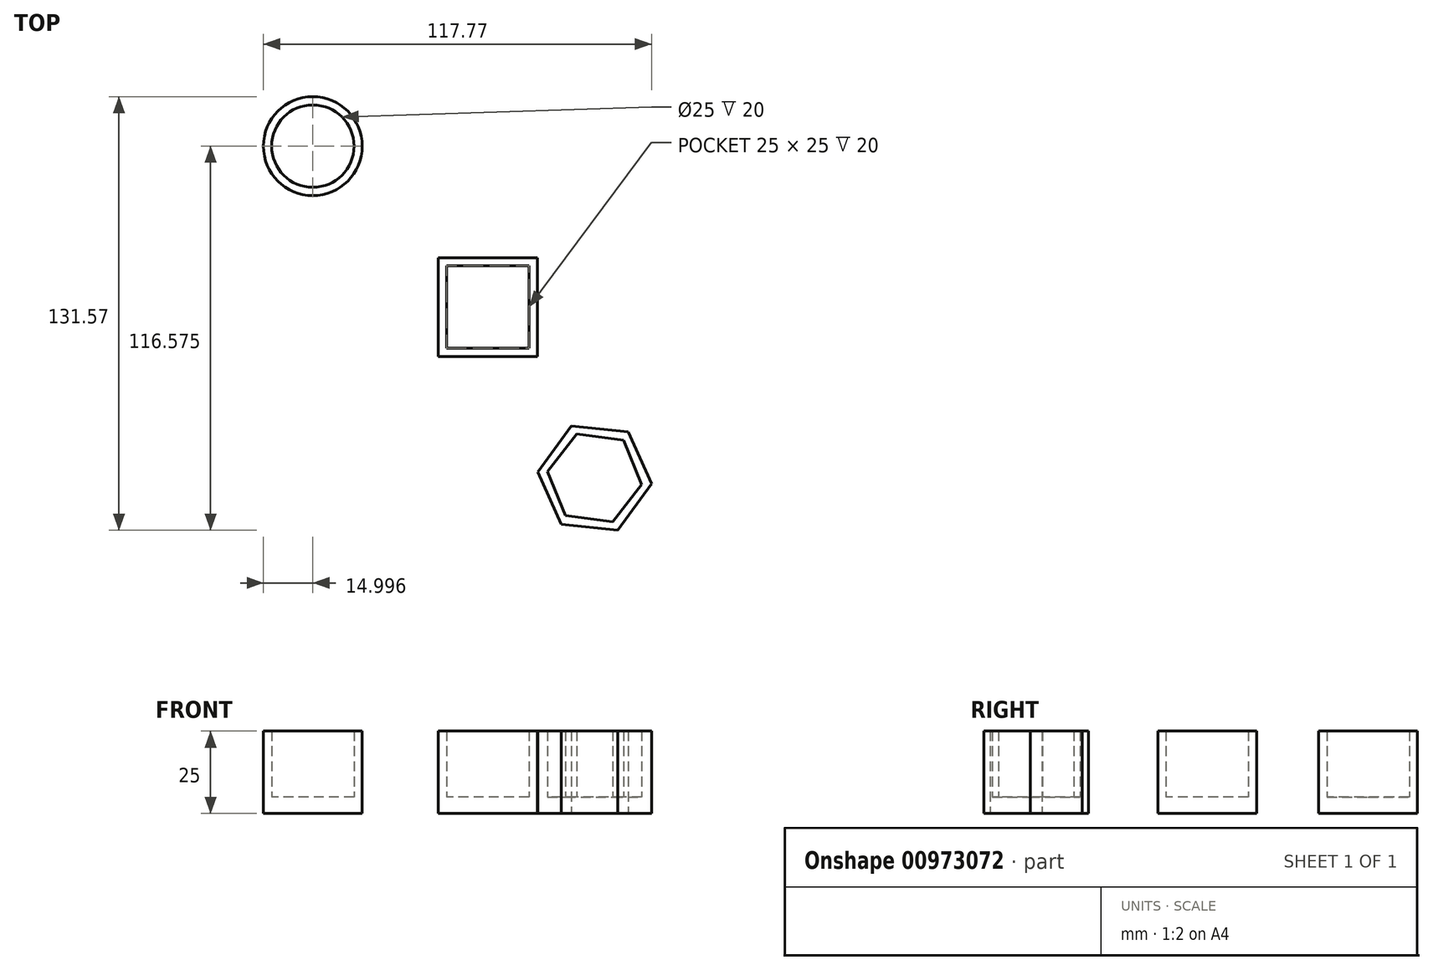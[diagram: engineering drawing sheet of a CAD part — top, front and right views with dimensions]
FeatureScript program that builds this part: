
annotation { "Feature Type Name" : "Feature", "Feature Type Description" : "" }
export const myFeature = defineFeature(function(context is Context, id is Id, definition is map)
    precondition{}
    {
        {
            var Q0;
            Q0=qCreatedBy(makeId("Top.planeOp"),FACE);
            var sketch = newSketch(context, id + "F0", { "sketchPlane" : qUnion([Q0])});
            skLineSegment(sketch, "E0.bottom", {"start": v(15, -15) * mm, "end": v(-15, -15) * mm});
            skLineSegment(sketch, "E0.top", {"start": v(15, 15) * mm, "end": v(-15, 15) * mm});
            skLineSegment(sketch, "E0.left", {"start": v(15, -15) * mm, "end": v(15, 15) * mm});
            skLineSegment(sketch, "E0.right", {"start": v(-15, -15) * mm, "end": v(-15, 15) * mm});
            skPoint(sketch, "E0.middle", {"position": v(0, 0) * mm});
            skLineSegment(sketch, "E1.bottom", {"start": v(-12.5, -12.5) * mm, "end": v(12.5, -12.5) * mm});
            skLineSegment(sketch, "E1.top", {"start": v(-12.5, 12.5) * mm, "end": v(12.5, 12.5) * mm});
            skLineSegment(sketch, "E1.left", {"start": v(-12.5, -12.5) * mm, "end": v(-12.5, 12.5) * mm});
            skLineSegment(sketch, "E1.right", {"start": v(12.5, -12.5) * mm, "end": v(12.5, 12.5) * mm});
            skSolve(sketch);
        }
        {
            var Q0;
            Q0=makeQuery(id+"F0.imprint","IMPRINT",FACE,{"disambiguationData":[TD([[makeQuery(id+"F0.imprint","IMPRINT",EDGE,{"derivedFrom":sQuery(id+"F0.wireOp",EDGE,"E0.bottom")}),-1.0]])]});
            var Q1;
            Q1=makeQuery(id+"F0.imprint","IMPRINT",FACE,{"disambiguationData":[TD([[makeQuery(id+"F0.imprint","IMPRINT",EDGE,{"derivedFrom":sQuery(id+"F0.wireOp",EDGE,"E1.bottom")}),1.0]])]});
            extrude(context, id + "F1", {"entities" : qUnion([Q0, Q1]), "depth" : 5 * mm, "offsetDistance" : 25 * mm});
        }
        {
            var Q0;
            Q0 = qSketchRegion(id + "F0", true);
            extrude(context, id + "F2", {"entities" : qUnion([Q0]), "operationType" : NewBodyOperationType.ADD, "depth" : 25 * mm, "offsetDistance" : 25 * mm});
        }
        {
            var Q0;
            Q0=qCreatedBy(makeId("Top.planeOp"),FACE);
            var sketch = newSketch(context, id + "F3", { "sketchPlane" : qUnion([Q0])});
            skCircle(sketch, "E2", {"center": v(-53.11, 48.86) * mm, "radius": 15 * mm});
            skCircle(sketch, "E3", {"center": v(-53.11, 48.86) * mm, "radius": 12.5 * mm});
            skSolve(sketch);
        }
        {
            var Q0;
            Q0=makeQuery(id+"F3.imprint","IMPRINT",FACE,{"disambiguationData":[TD([[makeQuery(id+"F3.imprint","IMPRINT",EDGE,{"derivedFrom":sQuery(id+"F3.wireOp",EDGE,"E3")}),1.0]])]});
            var Q1;
            Q1=makeQuery(id+"F3.imprint","IMPRINT",FACE,{"disambiguationData":[TD([[makeQuery(id+"F3.imprint","IMPRINT",EDGE,{"derivedFrom":sQuery(id+"F3.wireOp",EDGE,"E2")}),1.0]])]});
            extrude(context, id + "F4", {"entities" : qUnion([Q0, Q1]), "depth" : 5 * mm, "offsetDistance" : 25 * mm});
        }
        {
            var Q0;
            Q0 = qSketchRegion(id + "F3", true);
            extrude(context, id + "F5", {"entities" : qUnion([Q0]), "operationType" : NewBodyOperationType.ADD, "depth" : 25 * mm, "offsetDistance" : 25 * mm});
        }
        {
            var Q0;
            Q0=qCreatedBy(makeId("Top.planeOp"),FACE);
            var sketch = newSketch(context, id + "F6", { "sketchPlane" : qUnion([Q0])});
            skCircle(sketch, "E4.cCircle", {"center": v(32.43, -51.9) * mm, "radius": 15 * mm, "construction": true});
            skLineSegment(sketch, "E4.0", {"start": v(22.27, -65.92) * mm, "end": v(15.2, -50.1) * mm});
            skLineSegment(sketch, "E4.1", {"start": v(15.2, -50.1) * mm, "end": v(25.37, -36.08) * mm});
            skLineSegment(sketch, "E4.2", {"start": v(25.37, -36.08) * mm, "end": v(42.6, -37.87) * mm});
            skLineSegment(sketch, "E4.3", {"start": v(42.6, -37.87) * mm, "end": v(49.66, -53.68) * mm});
            skLineSegment(sketch, "E4.4", {"start": v(49.66, -53.68) * mm, "end": v(39.5, -67.7) * mm});
            skLineSegment(sketch, "E4.5", {"start": v(39.5, -67.7) * mm, "end": v(22.27, -65.92) * mm});
            skPoint(sketch, "E4.0.midPoint", {"position": v(18.74, -58) * mm});
            skCircle(sketch, "E5.cCircle", {"center": v(32.43, -51.9) * mm, "radius": 12.5 * mm, "construction": true});
            skLineSegment(sketch, "E5.0", {"start": v(23.62, -63.32) * mm, "end": v(18.13, -49.97) * mm});
            skLineSegment(sketch, "E5.1", {"start": v(18.13, -49.97) * mm, "end": v(26.94, -38.54) * mm});
            skLineSegment(sketch, "E5.2", {"start": v(26.94, -38.54) * mm, "end": v(41.25, -40.46) * mm});
            skLineSegment(sketch, "E5.3", {"start": v(41.25, -40.46) * mm, "end": v(46.74, -53.81) * mm});
            skLineSegment(sketch, "E5.4", {"start": v(46.74, -53.81) * mm, "end": v(37.92, -65.24) * mm});
            skLineSegment(sketch, "E5.5", {"start": v(37.92, -65.24) * mm, "end": v(23.62, -63.32) * mm});
            skPoint(sketch, "E5.0.midPoint", {"position": v(20.87, -56.64) * mm});
            skSolve(sketch);
        }
        {
            var Q0;
            Q0=makeQuery(id+"F6.imprint","IMPRINT",FACE,{"disambiguationData":[TD([[makeQuery(id+"F6.imprint","IMPRINT",EDGE,{"derivedFrom":sQuery(id+"F6.wireOp",EDGE,"E5.0")}),-1.0]])]});
            var Q1;
            Q1=makeQuery(id+"F6.imprint","IMPRINT",FACE,{"disambiguationData":[TD([[makeQuery(id+"F6.imprint","IMPRINT",EDGE,{"derivedFrom":sQuery(id+"F6.wireOp",EDGE,"E4.0")}),-1.0]])]});
            extrude(context, id + "F7", {"entities" : qUnion([Q0, Q1]), "depth" : 5 * mm, "offsetDistance" : 25 * mm});
        }
        {
            var Q0;
            Q0 = qSketchRegion(id + "F6", true);
            extrude(context, id + "F8", {"entities" : qUnion([Q0]), "operationType" : NewBodyOperationType.ADD, "depth" : 25 * mm, "offsetDistance" : 25 * mm});
        }
    });
